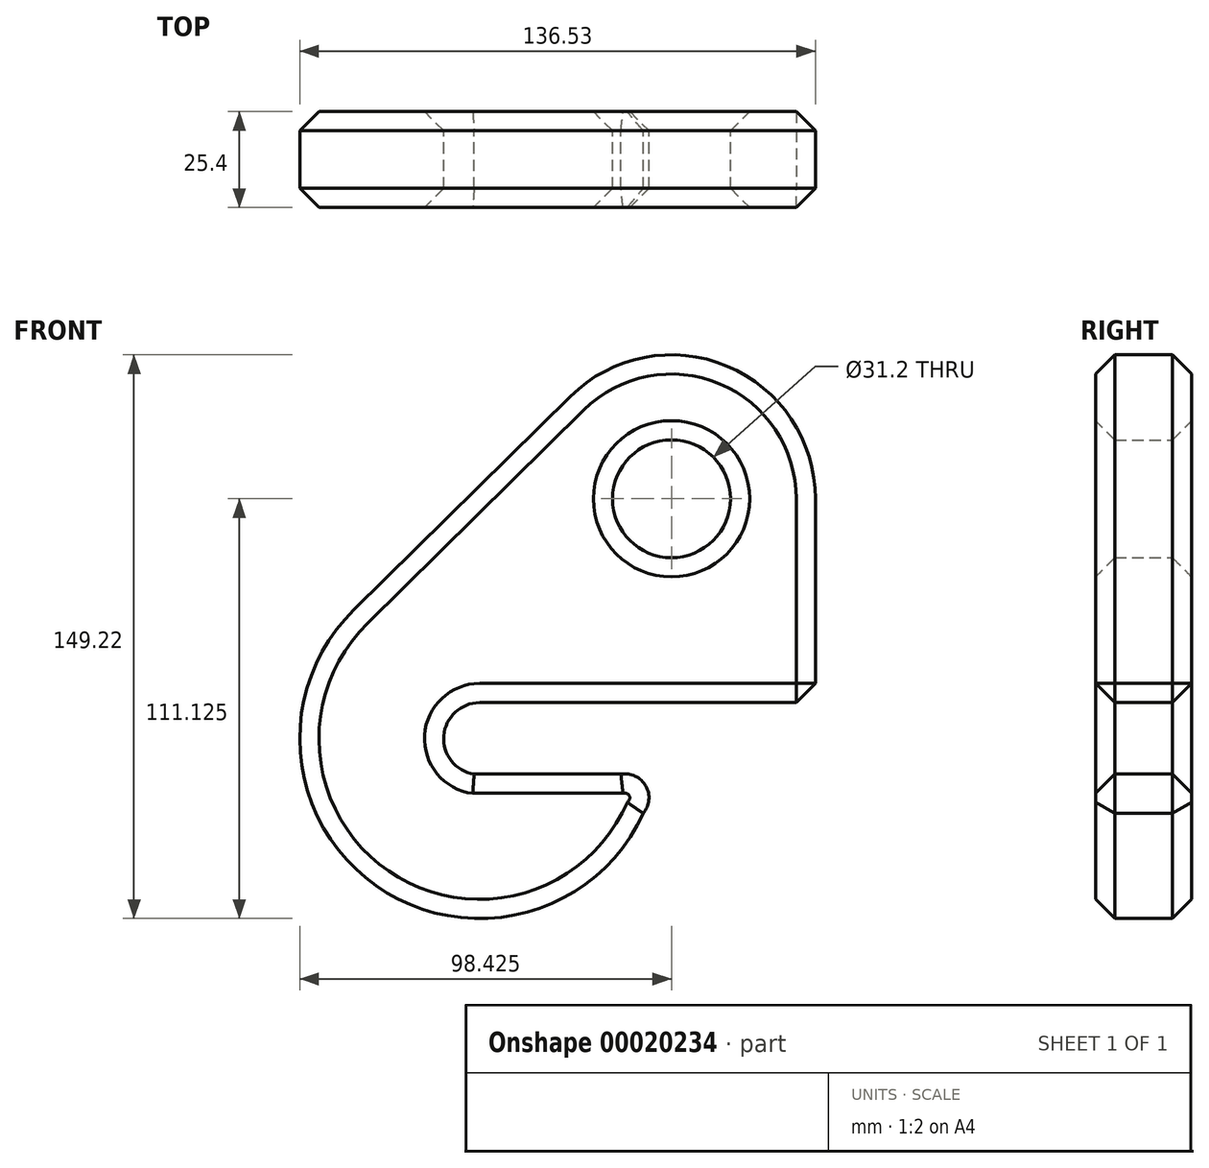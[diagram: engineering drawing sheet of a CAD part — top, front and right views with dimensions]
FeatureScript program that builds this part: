
annotation { "Feature Type Name" : "Feature", "Feature Type Description" : "" }
export const myFeature = defineFeature(function(context is Context, id is Id, definition is map)
    precondition{}
    {
        {
            var Q0;
            Q0=qCreatedBy(makeId("Front.planeOp"),FACE);
            var sketch = newSketch(context, id + "F0", { "sketchPlane" : qUnion([Q0])});
            skCircle(sketch, "E0", {"center": v(43.4, 39.2) * mm, "radius": 15.6 * mm});
            skArc(sketch, "E1", {"start": v(81.5, 39.2) * mm, "mid": v(58.1, 74.36) * mm, "end": v(16.65, 66.33) * mm});
            skLineSegment(sketch, "E2", {"start": v(-7.4, -14.77) * mm, "end": v(81.5, -14.77) * mm});
            skLineSegment(sketch, "E3", {"start": v(81.5, -14.77) * mm, "end": v(81.5, 39.2) * mm});
            skArc(sketch, "E4", {"start": v(-7.4, -14.77) * mm, "mid": v(-16.9, -25.03) * mm, "end": v(-5.93, -33.7) * mm});
            skLineSegment(sketch, "E5", {"start": v(-40.57, 9.87) * mm, "end": v(16.65, 66.33) * mm});
            skLineSegment(sketch, "E6", {"start": v(-8.86, -33.7) * mm, "end": v(32.13, -33.7) * mm});
            skPoint(sketch, "E7", {"position": v(39.3, -33.7) * mm});
            skArc(sketch, "E8", {"start": v(35.93, -44.07) * mm, "mid": v(36.6, -36.83) * mm, "end": v(30.04, -33.7) * mm});
            skPoint(sketch, "E8.first.point", {"position": v(30.04, -33.7) * mm});
            skPoint(sketch, "E8.second.point", {"position": v(35.93, -44.07) * mm});
            skPoint(sketch, "E8.third.point", {"position": v(25.32, -42.64) * mm});
            skArc(sketch, "E9.trimOffspring", {"start": v(-40.57, 9.87) * mm, "mid": v(-33.2, -64.32) * mm, "end": v(37.42, -40.42) * mm});
            skSolve(sketch);
        }
        {
            var Q0;
            {var subQ0=sQuery(id+"F0.wireOp",EDGE,"E6");var subQ1=sQuery(id+"F0.wireOp",EDGE,"E4");var subQ3=makeQuery(id+"F0.imprint","INTERSECT",VERTEX,{"disambiguationData":[OD(0.0)],"derivedFrom":[subQ1,subQ0]});Q0=makeQuery(id+"F0.imprint","IMPRINT",FACE,{"disambiguationData":[TD([[makeQuery(id+"F0.imprint","IMPRINT",EDGE,{"disambiguationData":[TD([[subQ3,1.0]])],"derivedFrom":subQ1}),1.0]])]});}
            var Q1;
            {var subQ0=sQuery(id+"F0.wireOp",EDGE,"E8");var subQ1=sQuery(id+"F0.wireOp",EDGE,"E6");var subQ3=makeQuery(id+"F0.imprint","INTERSECT",VERTEX,{"disambiguationData":[OD(0.0)],"derivedFrom":[subQ1,subQ0]});Q1=makeQuery(id+"F0.imprint","IMPRINT",FACE,{"disambiguationData":[TD([[makeQuery(id+"F0.imprint","IMPRINT",EDGE,{"disambiguationData":[TD([[subQ3,1.0]])],"derivedFrom":subQ1}),1.0]])]});}
            var Q2;
            {var subQ0=sQuery(id+"F0.wireOp",EDGE,"E9.trimOffspring");var subQ1=sQuery(id+"F0.wireOp",EDGE,"E8");var subQ3=makeQuery(id+"F0.imprint","INTERSECT",VERTEX,{"disambiguationData":[OD(0.0)],"derivedFrom":[subQ1,subQ0]});Q2=makeQuery(id+"F0.imprint","IMPRINT",FACE,{"disambiguationData":[TD([[makeQuery(id+"F0.imprint","IMPRINT",EDGE,{"disambiguationData":[TD([[subQ3,-1.0]])],"derivedFrom":subQ1}),1.0]])]});}
            var Q3;
            Q3=makeQuery(id+"F0.imprint","IMPRINT",FACE,{"disambiguationData":[TD([[makeQuery(id+"F0.imprint","IMPRINT",EDGE,{"derivedFrom":sQuery(id+"F0.wireOp",EDGE,"E0")}),-1.0]])]});
            extrude(context, id + "F1", {"entities" : qUnion([Q0, Q1, Q2, Q3]), "depth" : 25.4 * mm});
        }
        {
            var Q0;
            Q0=makeQuery(id+"F1.opExtrude","CAP_FACE",FACE,{"disambiguationData":[OSD([sQuery(id+"F0.wireOp",EDGE,"E0"),sQuery(id+"F0.wireOp",EDGE,"E1"),sQuery(id+"F0.wireOp",EDGE,"E2"),sQuery(id+"F0.wireOp",EDGE,"E3"),sQuery(id+"F0.wireOp",EDGE,"E4"),sQuery(id+"F0.wireOp",EDGE,"E5"),sQuery(id+"F0.wireOp",EDGE,"E6"),sQuery(id+"F0.wireOp",EDGE,"E8"),sQuery(id+"F0.wireOp",EDGE,"E9.trimOffspring")])],"isStart":false});
            var Q1;
            Q1=makeQuery(id+"F1.opExtrude","SWEPT_FACE",FACE,{"disambiguationData":[OSD([sQuery(id+"F0.wireOp",EDGE,"E1")])]});
            var Q2;
            Q2=makeQuery(id+"F1.opExtrude","SWEPT_FACE",FACE,{"disambiguationData":[OSD([sQuery(id+"F0.wireOp",EDGE,"E3")])]});
            var Q3;
            Q3=makeQuery(id+"F1.opExtrude","CAP_FACE",FACE,{"disambiguationData":[OSD([sQuery(id+"F0.wireOp",EDGE,"E0"),sQuery(id+"F0.wireOp",EDGE,"E1"),sQuery(id+"F0.wireOp",EDGE,"E2"),sQuery(id+"F0.wireOp",EDGE,"E3"),sQuery(id+"F0.wireOp",EDGE,"E4"),sQuery(id+"F0.wireOp",EDGE,"E5"),sQuery(id+"F0.wireOp",EDGE,"E6"),sQuery(id+"F0.wireOp",EDGE,"E8"),sQuery(id+"F0.wireOp",EDGE,"E9.trimOffspring")])],"isStart":true});
            var Q4;
            Q4=makeQuery(id+"F1.opExtrude","SWEPT_FACE",FACE,{"disambiguationData":[OSD([sQuery(id+"F0.wireOp",EDGE,"E0")])]});
            chamfer(context, id + "F2", {"entities" : qUnion([Q0, Q1, Q2, Q3, Q4]), "width" : 5.08 * mm, "tangentPropagation" : true});
        }
    });
